# Revit family: PRD_FrankeWS_PprTwlDspnsrs_EXOSPaperTowelDispenser_EXOS600EX_600EB_600EW
name_source: partatom
category: Specialty Equipment
revit_build: Autodesk Revit 2018 (Build: 20190510_1515(x64)
units: mm (PartAtom-declared; Revit-internal decimal feet)

## family parameters
Cut with Voids When Loaded = No
Host = Face
OmniClass Number = 23.40.20.21.17
OmniClass Title = Paper Towel Dispensers, Disposal Units
Part Type = Normal
Room Calculation Point = No
Round Connector Dimension = Use Diameter
Shared = No

## types (3) — shared parameters
AssetType = Fixed
Category = Pr_40_70_22_62, Paper Towel Dispensers
Default Elevation = 1200 mm
DispenserMaterial = PRD_AR_StainlessSteel_SatinFinished
DurationUnit = year
Features = stainless steel, surface satin finished
FillingQuantity = 400
FillingQuantityUom = Towels
Finish = satin finished
IfcExportAs = IfcFurnitureType
IfcExportType = USERDEFINED
IntegralAccessories = incl. mounting materials
IsBuiltIn = TRUE
Lock = Key-lock
MainColor = stainless steel
Manufacturer = KWC Group AG
ManufacturerName = KWC Group AG
ManufacturerURL = www.kwc.com
Material = stainless steel
MaterialCode = 1.4301
MaterialThickness = 1.20 mm
NBSDescription = Paper towel dispensers
NBSReference = 45-35-72/344
NominalDepth = 120 mm  [stored 0.393701 ft]
NominalHeight = 500 mm  [stored 1.64042 ft]
NominalWidth = 304 mm  [stored 0.997375 ft]
ProductInformation = https://pim.kwc.com
Size = 304 x 500 x 120 mm
Style = Dispenser
SurfaceTreatment = InoxPlus (anti fingerprint)
TypeOfConsumable = Paper towel
TypeOfFixing = Screw
TypeOfMounting = Recessed mounting
URL = www.kwc.com
Uniclass2015Code = Pr_40_70_22_62
Uniclass2015Title = Paper towel dispensers
Uniclass2015Version = Products v1.17
Version = 1
WarrantyDurationUnit = year

## per-type parameters (varying)
| type | BIMObjectName | Description | GrossWeight | ModelNumber | Name | NetWeight | PanelMaterial |
| EXOS600EX | PRD_AR_PaperTowelDispensers_EXOSPaperTowelDispenser_EXOS600EX | Paper towel dispenser for recessed mounting, stainless steel with satin finish, front and casing with InoxPlus surface refinement for the reduction of finger marks and better cleaning characteristics (easy to clean), material thickness 1.2 mm, capacity 300 - 400 pieces of Z-folded paper, includes mounting materials. | 5.14 kg | 2030034624 | Paper Towel Dispenser EXOS600EX | 4.14 kg | PRD_AR_StainlessSteel_SatinFinished |
| EXOS600EB | PRD_AR_PaperTowelDispensers_EXOSPaperTowelDispenser_EXOS600EB | Paper towel dispenser for recessed mounting, stainless steel with satin finish, black safety glass front panel, casing with InoxPlus surface refinement for the reduction of finger marks and better cleaning characteristics (easy to clean), material thickness 1.2 mm, capacity 300 - 400 pieces of Z-folded paper, includes mounting materials. | 5.78 kg | 2030034625 | Paper Towel Dispenser EXOS600EB | 4.78 kg | PRD_AR_Glass_Black |
| EXOS600EW | PRD_AR_PaperTowelDispensers_EXOSPaperTowelDispenser_EXOS600EW | Paper towel dispenser for recessed mounting, stainless steel with satin finish, white safety glass front panel, casing with InoxPlus surface refinement for the reduction of finger marks and better cleaning characteristics (easy to clean), material thickness 1.2 mm, capacity 300 - 400 pieces of Z-folded paper, includes mounting materials. | 5.78 kg | 2030034662 | Paper Towel Dispenser EXOS600EW | 4.78 kg | PRD_AR_Glass_White |

note: column(s) folded — value = type name in every type: Model, ModelReference

note: [stored X ft] marks values corroborated as IEEE doubles in the binary element streams (Revit-internal decimal feet)

## geometry (parser evidence)
native form markers: Sweep x6
no freeform markers — native parametric forms only
